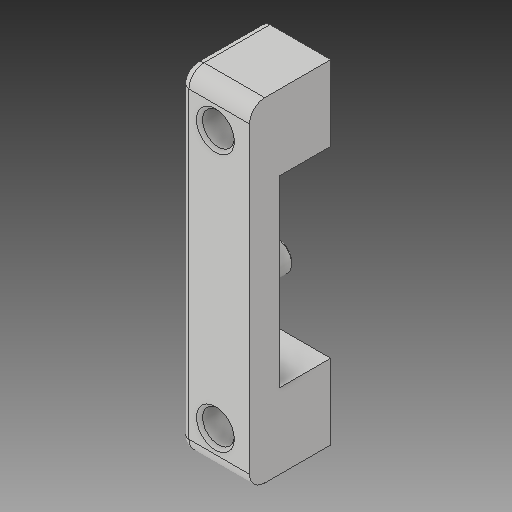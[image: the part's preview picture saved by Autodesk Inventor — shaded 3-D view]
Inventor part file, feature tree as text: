
AUTODESK INVENTOR PART (.ipt)
format: ipt  version: 2019 (Build 230136000, 136)  size: 178,176 bytes
history: native  units: mm
features: extrude x4, sketch x4, fillet x3, chamfer x1, pattern_linear x1
ambient origin geometry x8: Origin, YZ Plane, XZ Plane, XY Plane, X Axis, Y Axis, Z Axis, Center Point
bodies: Solid1 (feature_tree)
feature tree (13):
  extrude  "Extrusion1"  Depth=22.0mm
  extrude  "Extrusion2"  Depth=12.1mm
  extrude  "Extrusion3"  Depth=2.0mm TaperAngle=0.0deg
  fillet  "Fillet1"  Radius=0.65mm
  fillet  "Fillet2"  Radius=1.95mm
  extrude  "Extrusion4"  Depth=0.1mm
  chamfer  "Chamfer1"  Distance=1.0mm
  pattern_linear  "Rectangular Pattern1"  Spacing1=8.5mm  [1 undecoded]
  fillet  "Fillet3"  Radius=2.1mm
  sketch  "Sketch1"  dims[d0=4.5mm d1=22.0mm]
  sketch  "Sketch2"  dims[d2=4.5mm d3=12.1mm]
  sketch  "Sketch3"  dims[d4=3.35mm d5=0.0mm d6=2.0mm d7=0.0mm d8=0.65mm d9=1.95mm]
  sketch  "Sketch4"  dims[d10=1.5mm d11=0.0mm d12=0.1mm d13=1.0mm d14=8.5mm d15=2.1mm d16=6.0mm d17=0.0mm d18=0.2mm d19=2.0mm d20=45.0deg d21=20.0mm d23=17.0mm d24=0.5mm]
note: 1 required parameter value undecoded (feature->parameter linkage not recoverable at this tier; creation-order binding heuristic only, values carry confidence <= 0.55)
